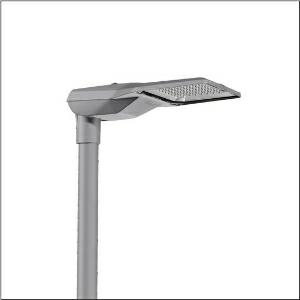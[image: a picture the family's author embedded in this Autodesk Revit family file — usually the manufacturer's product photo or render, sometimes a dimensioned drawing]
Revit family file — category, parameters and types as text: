
# Revit family: streetlight_sl_21_midi___stw1_0a_5xe3e33s08lb_8a64
name_source: partatom
category: Lighting Fixtures
units: mm (PartAtom-declared; Revit-internal decimal feet)

## family parameters
Cut with Voids When Loaded = No
Host = Face
Light Source = No
Part Type = Normal
Room Calculation Point = No
Round Connector Dimension = Use Diameter
Shared = No

## types (1)
- --- (1 x LED, 14340 lm, 99.6 W, 3000K)
    Apparent Load = 100 VA
    CIE Flux Codes = 38 75 98 100 100
    Color Rendering = 70
    Color Temperature = 3000K
    Default Elevation = 1800 mm
    Description = Streetlight SL 21 midi, mast luminaire, primary light control with lens, of PMMA, primary optical cover: cover, of toughened safety glass, transparent, light distribution: STW1.0a, light emission: direct distribution, primary light characteristic: asymmetric, installation type: side-entry, post-top, LED, High Power LED, rated luminous flux: 14.340lm, luminous efficacy: 144lm/W, light colour: 730, colour temperature: 3000K, control gear: D4i, control: overheat protection, constant luminous flux control, time-dependent luminous flux control, flexible luminous flux parameterisation, pre-setting: logarithmic dimming characteristic, mains connection: 230..240V, AC, 50/60Hz, start of lifetime: 100W, end of service life: 102W, reduction: 46W, luminaire housing, of diecast aluminium, powder-coated, SITECO metallic grey (DB 702S), corrosivity category C5 high according to DIN EN ISO 12944, please order mast flange separately, inclination adjustable: 0°, 5°, 10°, 15°, sealing non-destructively replaceable, multi-level sealing system, length: 644mm, width: 335mm, height: 110mm, mast flange for spigot size: 42mm (side-entry): 5XC10008XM4, 60/48mm (side-entry/post-top): 5XC10108XM2, 76/60mm (side-entry/post-top): 5XC10108XM1, mounting height: 4..8m, Smart Interface above, protection rating (complete): IP66, insulation class (complete): insulation class II (safety insulation), certification: CE, ENEC, ENEC+, VDE, impact resistance: IK10, permissible operating ambient temperature for outdoor applications: -40..+50°C, standard-compliant lighting for roads and squares, packaging unit: 1 piece

Light Distribution: STW1.0a
    Height = 111 mm
    Lamp = 1 x LED
    Lamp Light Flux = 14340 lm
    Lamp Power = 99.6 W
    Lamp count = 1
    Length = 644 mm
    Luminous efficacy = 144 lm/W
    Manufacturer = Siteco
    ModVariant = No
    Model = 5XE3E33S08LB
    Number of Poles = 1
    OnlyDefault = Yes
    Power Factor = 1
    Product Name = Streetlight SL 21 midi | STW1.0a
    Product group = mast luminaire | pylon top
    ProductGroupID = 6100
    Protection Class = Protection class II
    Protection Degree = IP 66
    RLX_Detail_Level = 1
    RLX_Emergency_Light_Flux = 0 lm
    RLX_Emergency_Type = 0
    RLX_Emergency_Type_DB = No
    RlxData = <blob elided: 26841 chars, md5=51039a85>
    Socket = socket
    Standby Power = 0 W
    System Light Flux = 14340 lm
    System Power = 100 W
    Type Comments = factory setting: luminous flux: 100 % | dim-lin: 254 | 1020 mA
    Type Image = l_1004302.jpg
    URL = http://relux.com
    VarID = @adj_031463
    Voltage = 0 V
    Weight = 0.00 kg
    Width = 336 mm

## geometry (parser evidence)
native form markers: Blend x4, Sweep x12
no freeform markers — native parametric forms only
